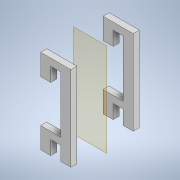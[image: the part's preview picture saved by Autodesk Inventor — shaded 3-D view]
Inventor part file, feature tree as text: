
AUTODESK INVENTOR PART (.ipt)
format: ipt  version: 2020.2 (Build 242310000, 310)  size: 143,360 bytes
history: native  units: in
note: dims shown in document units (in); Inventor stores cm internally (conversion verified against a paired STEP export)
features: extrude x1, plane x1, mirror x1, sketch x1
ambient origin geometry x8: Origin, YZ Plane, XZ Plane, XY Plane, X Axis, Y Axis, Z Axis, Center Point
bodies: Solid1 (feature_tree)
feature tree (4):
  extrude  "Extrusion1"  Depth=0.175in
  plane  "Work Plane1"
  mirror  "Mirror1"
  sketch  "Sketch1"  dims[d1=1.4in d2=0.175in d3=0.175in d4=0.25in d6=0.25in d7=0.25in d11=0.15in d12=0.0in d13=0.525in d14=0.525in d15=0.775in]
